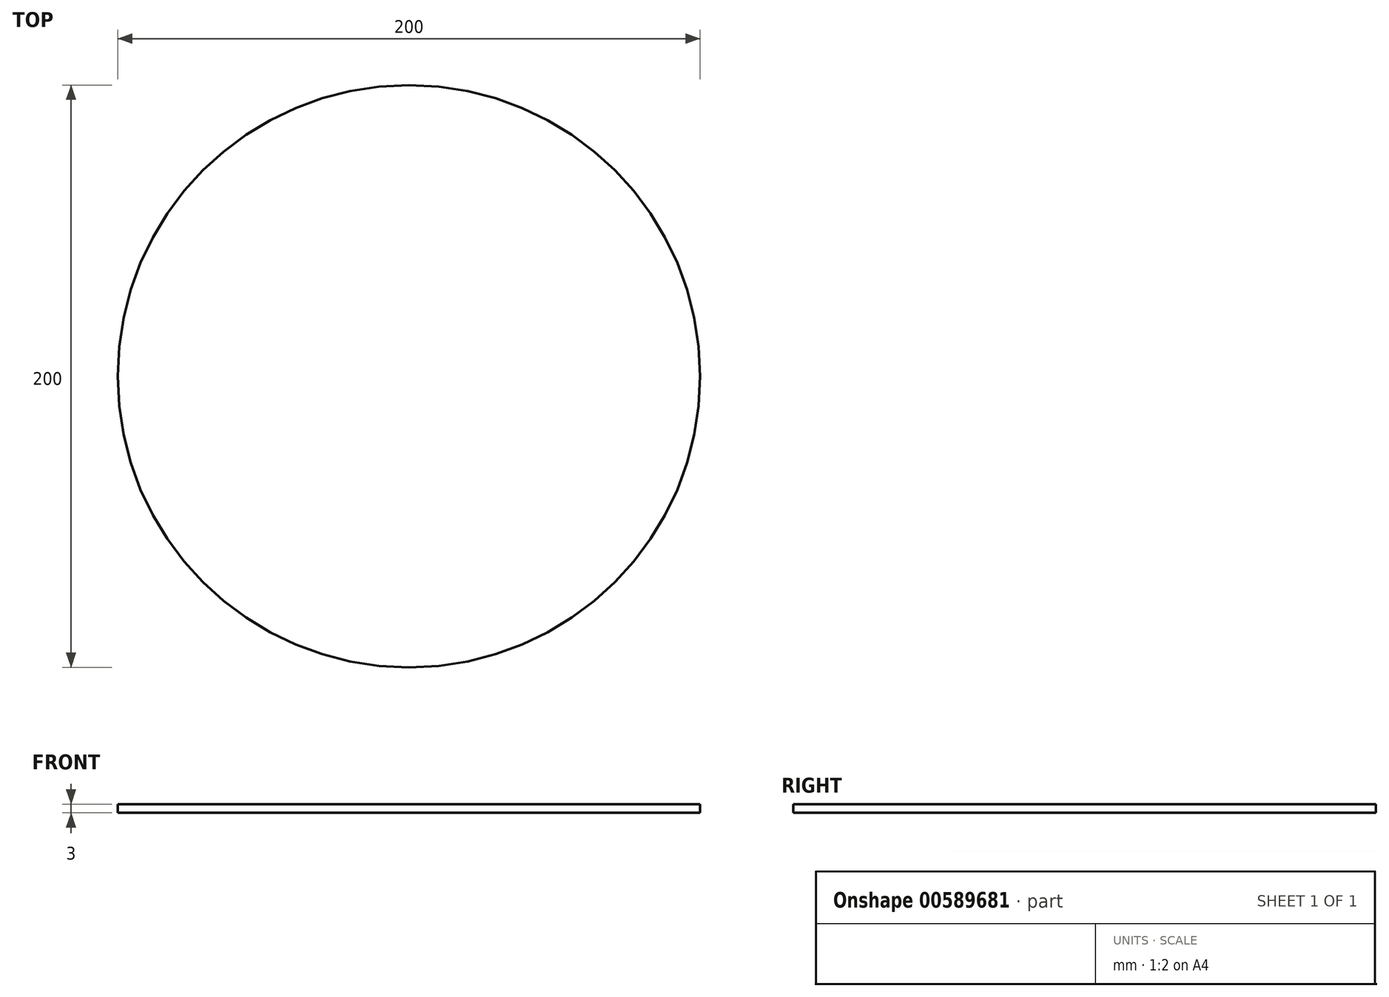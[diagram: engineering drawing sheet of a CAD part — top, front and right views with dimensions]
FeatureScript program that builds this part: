
annotation { "Feature Type Name" : "Feature", "Feature Type Description" : "" }
export const myFeature = defineFeature(function(context is Context, id is Id, definition is map)
    precondition{}
    {
        {
            var Q0;
            Q0=qCreatedBy(makeId("Top.planeOp"),FACE);
            var sketch = newSketch(context, id + "F0", { "sketchPlane" : qUnion([Q0])});
            skCircle(sketch, "E0", {"center": v(0, 0) * mm, "radius": 100 * mm});
            skSolve(sketch);
        }
        {
            var Q0;
            Q0 = qSketchRegion(id + "F0", true);
            extrude(context, id + "F1", {"entities" : qUnion([Q0]), "depth" : 3 * mm, "offsetDistance" : 25 * mm});
        }
    });
